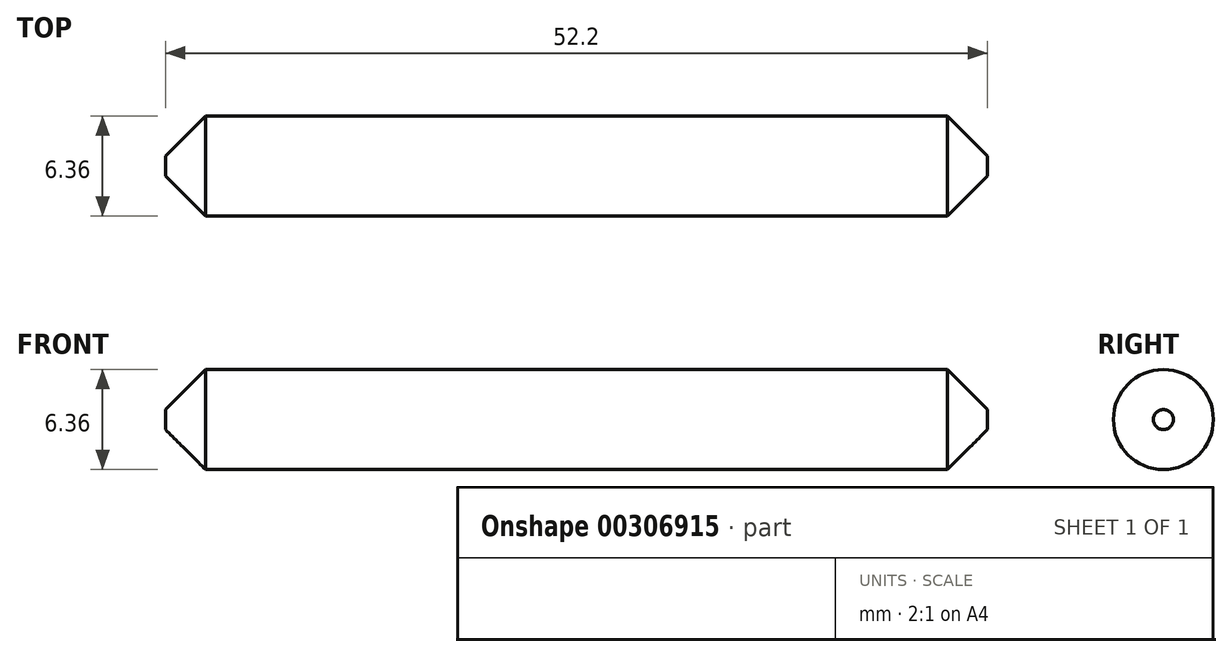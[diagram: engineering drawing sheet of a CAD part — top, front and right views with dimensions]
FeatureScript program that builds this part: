
annotation { "Feature Type Name" : "Feature", "Feature Type Description" : "" }
export const myFeature = defineFeature(function(context is Context, id is Id, definition is map)
    precondition{}
    {
        {
            var Q0;
            Q0=qCreatedBy(makeId("Right.planeOp"),FACE);
            var sketch = newSketch(context, id + "F0", { "sketchPlane" : qUnion([Q0])});
            skCircle(sketch, "E0", {"center": v(0, 0) * mm, "radius": 3.18 * mm});
            skSolve(sketch);
        }
        {
            var Q0;
            Q0=makeQuery(id+"F0.imprint","IMPRINT",FACE,{"disambiguationData":[TD([[makeQuery(id+"F0.imprint","IMPRINT",EDGE,{"derivedFrom":sQuery(id+"F0.wireOp",EDGE,"E0")}),1.0]])]});
            extrude(context, id + "F1", {"entities" : qUnion([Q0]), "oppositeDirection" : true, "depth" : 52.2 * mm});
        }
        {
            var Q0;
            Q0=makeQuery(id+"F1.opExtrude","CAP_FACE",FACE,{"disambiguationData":[OSD([sQuery(id+"F0.wireOp",EDGE,"E0")])],"isStart":true});
            var Q1;
            Q1=makeQuery(id+"F1.opExtrude","CAP_FACE",FACE,{"disambiguationData":[OSD([sQuery(id+"F0.wireOp",EDGE,"E0")])],"isStart":false});
            chamfer(context, id + "F2", {"entities" : qUnion([Q0, Q1]), "chamferType" : ChamferType.OFFSET_ANGLE, "width" : 2.54 * mm, "oppositeDirection" : false, "angle" : 45 * degree, "tangentPropagation" : true});
        }
    });
